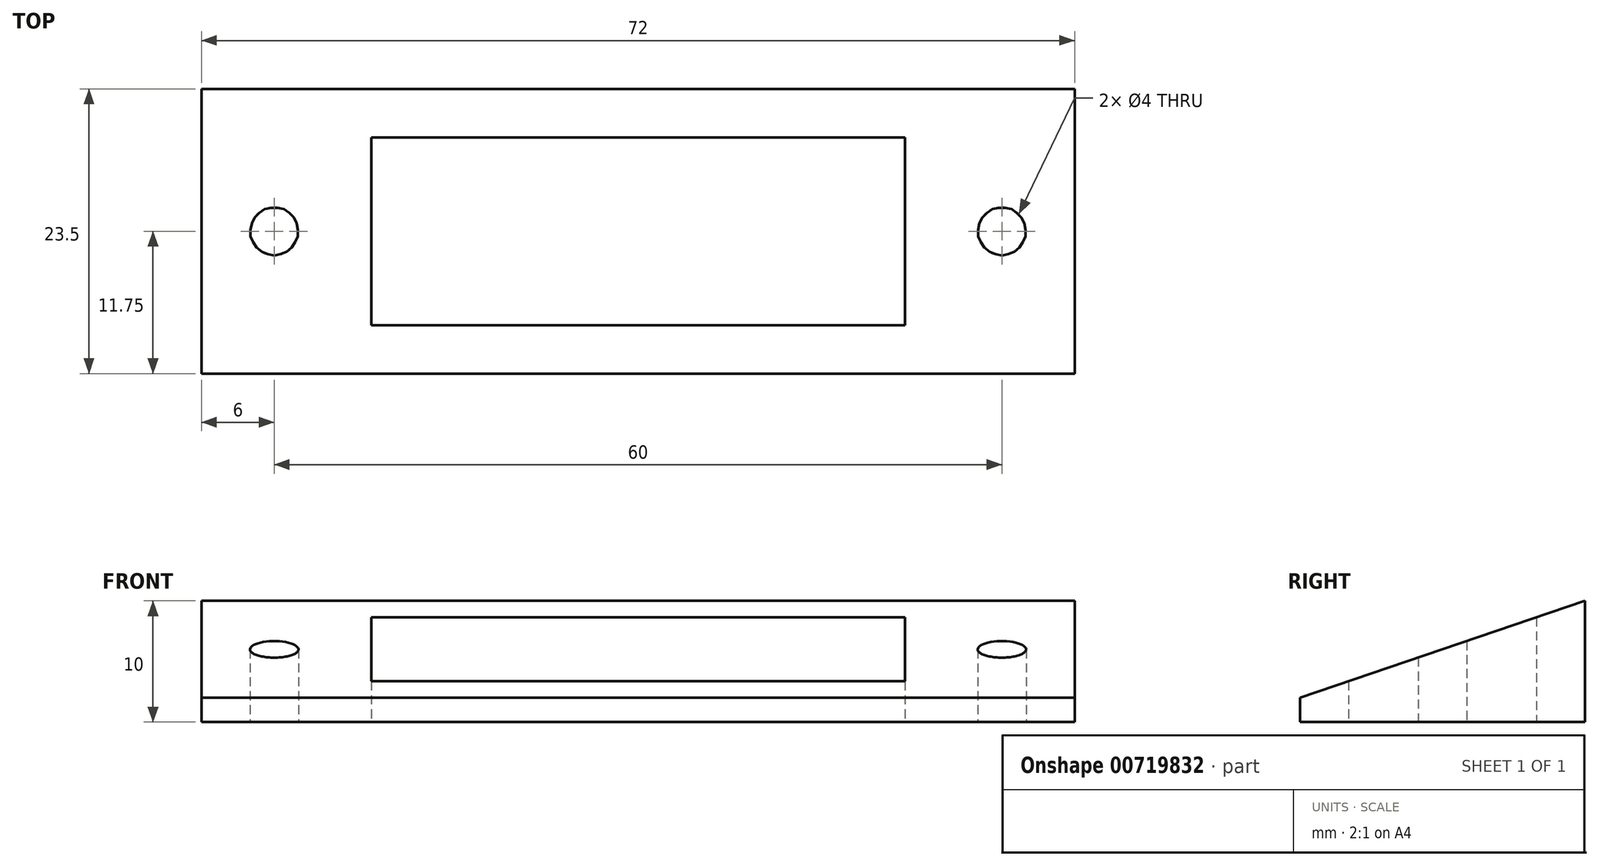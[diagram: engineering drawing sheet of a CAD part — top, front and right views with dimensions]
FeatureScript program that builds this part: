
annotation { "Feature Type Name" : "Feature", "Feature Type Description" : "" }
export const myFeature = defineFeature(function(context is Context, id is Id, definition is map)
    precondition{}
    {
        {
            var Q0;
            Q0=qCreatedBy(makeId("Top.planeOp"),FACE);
            var sketch = newSketch(context, id + "F0", { "sketchPlane" : qUnion([Q0])});
            skLineSegment(sketch, "E0.bottom", {"start": v(0, 0) * mm, "end": v(72, 0) * mm});
            skLineSegment(sketch, "E0.top", {"start": v(0, -23.5) * mm, "end": v(72, -23.5) * mm});
            skLineSegment(sketch, "E0.left", {"start": v(0, 0) * mm, "end": v(0, -23.5) * mm});
            skLineSegment(sketch, "E0.right", {"start": v(72, 0) * mm, "end": v(72, -23.5) * mm});
            skLineSegment(sketch, "E1.bottom", {"start": v(14, -4) * mm, "end": v(58, -4) * mm});
            skLineSegment(sketch, "E1.top", {"start": v(14, -19.5) * mm, "end": v(58, -19.5) * mm});
            skLineSegment(sketch, "E1.left", {"start": v(14, -4) * mm, "end": v(14, -19.5) * mm});
            skLineSegment(sketch, "E1.right", {"start": v(58, -4) * mm, "end": v(58, -19.5) * mm});
            skCircle(sketch, "E2", {"center": v(6, -11.75) * mm, "radius": 2 * mm});
            skCircle(sketch, "E3", {"center": v(66, -11.75) * mm, "radius": 2 * mm});
            skSolve(sketch);
        }
        {
            var Q0;
            Q0=makeQuery(id+"F0.imprint","IMPRINT",FACE,{"disambiguationData":[TD([[makeQuery(id+"F0.imprint","IMPRINT",EDGE,{"derivedFrom":sQuery(id+"F0.wireOp",EDGE,"E0.bottom")}),-1.0]])]});
            extrude(context, id + "F1", {"entities" : qUnion([Q0]), "depth" : 2 * mm, "offsetDistance" : 25 * mm});
        }
        {
            var Q0;
            Q0=makeQuery(id+"F1.opExtrude","CAP_FACE",FACE,{"disambiguationData":[OSD([sQuery(id+"F0.wireOp",EDGE,"E0.bottom"),sQuery(id+"F0.wireOp",EDGE,"E0.top"),sQuery(id+"F0.wireOp",EDGE,"E0.left"),sQuery(id+"F0.wireOp",EDGE,"E0.right"),sQuery(id+"F0.wireOp",EDGE,"E1.bottom"),sQuery(id+"F0.wireOp",EDGE,"E1.top"),sQuery(id+"F0.wireOp",EDGE,"E1.left"),sQuery(id+"F0.wireOp",EDGE,"E1.right"),sQuery(id+"F0.wireOp",EDGE,"E2"),sQuery(id+"F0.wireOp",EDGE,"E3")])],"isStart":false});
            extrude(context, id + "F2", {"entities" : qUnion([Q0]), "operationType" : NewBodyOperationType.ADD, "depth" : 8 * mm, "offsetDistance" : 25 * mm});
        }
        {
            var Q0;
            Q0=makeQuery(id+"F2.opExtrude","CAP_EDGE",EDGE,{"disambiguationData":[OSD([sQuery(id+"F0.wireOp",EDGE,"E0.top")])],"isStart":false});
            chamfer(context, id + "F3", {"entities" : qUnion([Q0]), "chamferType" : ChamferType.TWO_OFFSETS, "width1" : 23.5 * mm, "oppositeDirection" : false, "width2" : 8 * mm, "tangentPropagation" : true});
        }
    });
